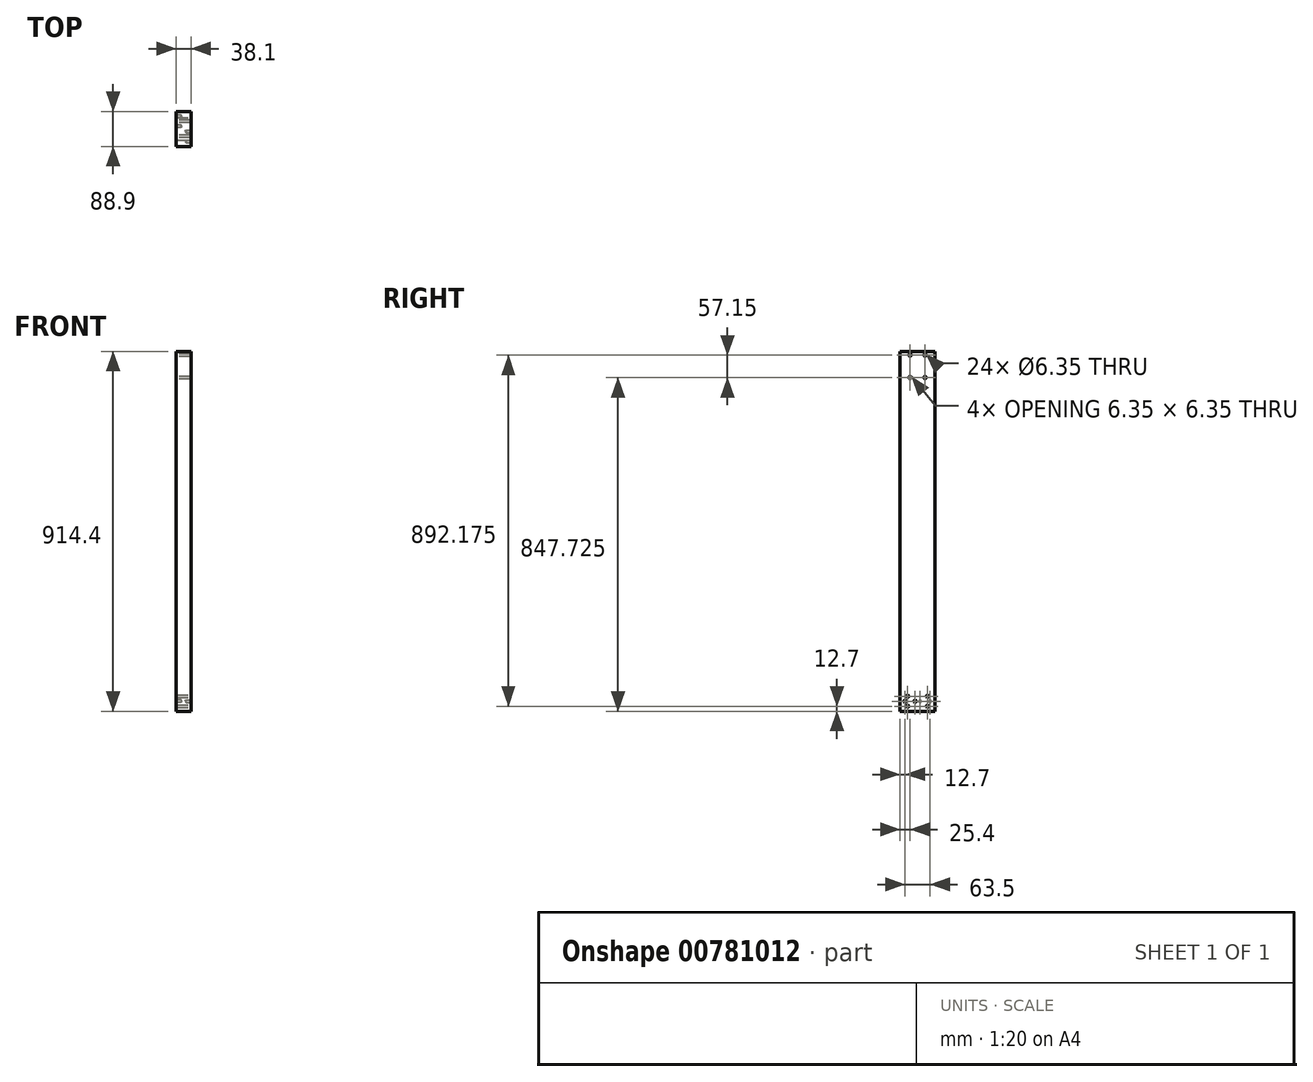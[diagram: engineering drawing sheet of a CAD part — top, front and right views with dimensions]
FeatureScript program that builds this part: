
annotation { "Feature Type Name" : "Feature", "Feature Type Description" : "" }
export const myFeature = defineFeature(function(context is Context, id is Id, definition is map)
    precondition{}
    {
        {
            var Q0;
            Q0=qCreatedBy(makeId("Right.planeOp"),FACE);
            var sketch = newSketch(context, id + "F0", { "sketchPlane" : qUnion([Q0])});
            skLineSegment(sketch, "E0.bottom", {"start": v(0, 0) * mm, "end": v(88.9, 0) * mm});
            skLineSegment(sketch, "E0.top", {"start": v(0, -914.4) * mm, "end": v(88.9, -914.4) * mm});
            skLineSegment(sketch, "E0.left", {"start": v(0, 0) * mm, "end": v(0, -914.4) * mm});
            skLineSegment(sketch, "E0.right", {"start": v(88.9, 0) * mm, "end": v(88.9, -914.4) * mm});
            skSolve(sketch);
        }
        {
            var Q0;
            Q0=makeQuery(id+"F0.imprint","IMPRINT",FACE,{"disambiguationData":[TD([[makeQuery(id+"F0.imprint","IMPRINT",EDGE,{"derivedFrom":sQuery(id+"F0.wireOp",EDGE,"E0.bottom")}),-1.0]])]});
            extrude(context, id + "F1", {"entities" : qUnion([Q0]), "depth" : 38.1 * mm, "offsetDistance" : 25.4 * mm});
        }
        {
            var Q0;
            Q0=makeQuery(id+"F1.opExtrude","CAP_FACE",FACE,{"disambiguationData":[OSD([sQuery(id+"F0.wireOp",EDGE,"E0.bottom"),sQuery(id+"F0.wireOp",EDGE,"E0.top"),sQuery(id+"F0.wireOp",EDGE,"E0.left"),sQuery(id+"F0.wireOp",EDGE,"E0.right")])],"isStart":true});
            var sketch = newSketch(context, id + "F2", { "sketchPlane" : qUnion([Q0])});
            skLineSegment(sketch, "E1", {"start": v(-63.5, 47.63) * mm, "end": v(-63.5, -66.68) * mm, "construction": true});
            skPoint(sketch, "E2", {"position": v(-63.5, -9.53) * mm});
            skLineSegment(sketch, "E3", {"start": v(-25.4, 0) * mm, "end": v(-25.4, -66.68) * mm, "construction": true});
            skLineSegment(sketch, "E4", {"start": v(-63.5, -9.53) * mm, "end": v(-25.4, -9.52) * mm, "construction": true});
            skPoint(sketch, "E5", {"position": v(-25.4, -9.52) * mm});
            skPoint(sketch, "E6", {"position": v(-25.4, -66.68) * mm});
            skPoint(sketch, "E7", {"position": v(-63.5, -66.68) * mm});
            skSolve(sketch);
        }
        {
            var Q0;
            Q0=sQuery(id+"F2.wireOp",VERTEX,"E2");
            var Q1;
            Q1=sQuery(id+"F2.wireOp",VERTEX,"E5");
            var Q2;
            Q2=sQuery(id+"F2.wireOp",VERTEX,"E7");
            var Q3;
            Q3=sQuery(id+"F2.wireOp",VERTEX,"E6");
            var Q4;
            Q4=makeQuery(id+"F1.opExtrude","SWEPT_BODY",BODY,{"disambiguationData":[OSD([sQuery(id+"F0.wireOp",EDGE,"E0.bottom"),sQuery(id+"F0.wireOp",EDGE,"E0.top"),sQuery(id+"F0.wireOp",EDGE,"E0.left"),sQuery(id+"F0.wireOp",EDGE,"E0.right")])]});
            hole(context, id + "F3", {"style" : HoleStyle.SIMPLE, "endStyle" : HoleEndStyle.THROUGH, "holeDiameter" : 6.35 * mm, "majorDiameter" : 6.35 * mm, "isTappedThrough" : true, "tappedDepth" : 12.7 * mm, "tapClearance" : 3, "locations" : qUnion([Q0, Q1, Q2, Q3]), "scope" : qUnion([Q4])});
        }
        {
            var Q0;
            Q0=makeQuery(id+"F1.opExtrude","CAP_FACE",FACE,{"disambiguationData":[OSD([sQuery(id+"F0.wireOp",EDGE,"E0.bottom"),sQuery(id+"F0.wireOp",EDGE,"E0.top"),sQuery(id+"F0.wireOp",EDGE,"E0.left"),sQuery(id+"F0.wireOp",EDGE,"E0.right")])],"isStart":false});
            var sketch = newSketch(context, id + "F4", { "sketchPlane" : qUnion([Q0])});
            skLineSegment(sketch, "E8", {"start": v(0, -876.3) * mm, "end": v(88.9, -876.3) * mm, "construction": true});
            skLineSegment(sketch, "E9", {"start": v(0, -901.7) * mm, "end": v(88.9, -901.7) * mm, "construction": true});
            skPoint(sketch, "E10", {"position": v(19.05, -876.3) * mm});
            skPoint(sketch, "E11", {"position": v(19.05, -901.7) * mm});
            skPoint(sketch, "E12", {"position": v(69.85, -876.3) * mm});
            skPoint(sketch, "E13", {"position": v(69.85, -901.7) * mm});
            skPoint(sketch, "E14", {"position": v(47, -876.3) * mm});
            skPoint(sketch, "E15", {"position": v(31.75, -901.7) * mm});
            skPoint(sketch, "E16", {"position": v(41.91, -876.3) * mm});
            skPoint(sketch, "E17", {"position": v(57.15, -901.7) * mm});
            skSolve(sketch);
        }
        {
            var Q0;
            Q0=sQuery(id+"F4.wireOp",VERTEX,"E10");
            var Q1;
            Q1=sQuery(id+"F4.wireOp",VERTEX,"E11");
            var Q2;
            Q2=sQuery(id+"F4.wireOp",VERTEX,"E12");
            var Q3;
            Q3=sQuery(id+"F4.wireOp",VERTEX,"E13");
            var Q4;
            Q4=makeQuery(id+"F1.opExtrude","SWEPT_BODY",BODY,{"disambiguationData":[OSD([sQuery(id+"F0.wireOp",EDGE,"E0.bottom"),sQuery(id+"F0.wireOp",EDGE,"E0.top"),sQuery(id+"F0.wireOp",EDGE,"E0.left"),sQuery(id+"F0.wireOp",EDGE,"E0.right")])]});
            hole(context, id + "F5", {"style" : HoleStyle.SIMPLE, "endStyle" : HoleEndStyle.THROUGH, "holeDiameter" : 6.35 * mm, "majorDiameter" : 6.35 * mm, "isTappedThrough" : true, "tappedDepth" : 12.7 * mm, "tapClearance" : 3, "locations" : qUnion([Q0, Q1, Q2, Q3]), "scope" : qUnion([Q4])});
        }
        {
            var Q0;
            Q0=makeQuery(id+"F1.opExtrude","CAP_FACE",FACE,{"disambiguationData":[OSD([sQuery(id+"F0.wireOp",EDGE,"E0.bottom"),sQuery(id+"F0.wireOp",EDGE,"E0.top"),sQuery(id+"F0.wireOp",EDGE,"E0.left"),sQuery(id+"F0.wireOp",EDGE,"E0.right")])],"isStart":true});
            var sketch = newSketch(context, id + "F6", { "sketchPlane" : qUnion([Q0])});
            skLineSegment(sketch, "E18", {"start": v(0, -889) * mm, "end": v(-88.9, -889) * mm, "construction": true});
            skLineSegment(sketch, "E19", {"start": v(-76.2, -914.4) * mm, "end": v(-76.2, -889) * mm, "construction": true});
            skLineSegment(sketch, "E20", {"start": v(-50.8, -914.4) * mm, "end": v(-50.8, -889) * mm, "construction": true});
            skSolve(sketch);
        }
        {
            var Q0;
            Q0=sQuery(id+"F6.wireOp",VERTEX,"E19.end");
            var Q1;
            Q1=sQuery(id+"F6.wireOp",VERTEX,"E20.end");
            var Q2;
            Q2=makeQuery(id+"F1.opExtrude","SWEPT_BODY",BODY,{"disambiguationData":[OSD([sQuery(id+"F0.wireOp",EDGE,"E0.bottom"),sQuery(id+"F0.wireOp",EDGE,"E0.top"),sQuery(id+"F0.wireOp",EDGE,"E0.left"),sQuery(id+"F0.wireOp",EDGE,"E0.right")])]});
            hole(context, id + "F7", {"style" : HoleStyle.SIMPLE, "endStyle" : HoleEndStyle.BLIND, "holeDiameter" : 6.35 * mm, "majorDiameter" : 6.35 * mm, "holeDepth" : 12.7 * mm, "isTappedThrough" : true, "tappedDepth" : 12.7 * mm, "tapClearance" : 3, "locations" : qUnion([Q0, Q1]), "scope" : qUnion([Q2])});
        }
        {
            var Q0;
            Q0=makeQuery(id+"F1.opExtrude","CAP_FACE",FACE,{"disambiguationData":[OSD([sQuery(id+"F0.wireOp",EDGE,"E0.bottom"),sQuery(id+"F0.wireOp",EDGE,"E0.top"),sQuery(id+"F0.wireOp",EDGE,"E0.left"),sQuery(id+"F0.wireOp",EDGE,"E0.right")])],"isStart":false});
            var sketch = newSketch(context, id + "F8", { "sketchPlane" : qUnion([Q0])});
            skLineSegment(sketch, "E21", {"start": v(0, -889) * mm, "end": v(88.9, -889) * mm, "construction": true});
            skPoint(sketch, "E22", {"position": v(38.1, -889) * mm});
            skPoint(sketch, "E23", {"position": v(12.7, -889) * mm});
            skLineSegment(sketch, "E24", {"start": v(44.45, -914.4) * mm, "end": v(44.45, -846.91) * mm, "construction": true});
            skSolve(sketch);
        }
        {
            var Q0;
            Q0=sQuery(id+"F8.wireOp",VERTEX,"E23");
            var Q1;
            Q1=sQuery(id+"F8.wireOp",VERTEX,"E22");
            var Q2;
            Q2=makeQuery(id+"F1.opExtrude","SWEPT_BODY",BODY,{"disambiguationData":[OSD([sQuery(id+"F0.wireOp",EDGE,"E0.bottom"),sQuery(id+"F0.wireOp",EDGE,"E0.top"),sQuery(id+"F0.wireOp",EDGE,"E0.left"),sQuery(id+"F0.wireOp",EDGE,"E0.right")])]});
            hole(context, id + "F9", {"style" : HoleStyle.SIMPLE, "endStyle" : HoleEndStyle.BLIND, "holeDiameter" : 6.35 * mm, "majorDiameter" : 6.35 * mm, "holeDepth" : 12.7 * mm, "isTappedThrough" : true, "tappedDepth" : 12.7 * mm, "tapClearance" : 3, "locations" : qUnion([Q0, Q1]), "scope" : qUnion([Q2])});
        }
    });
